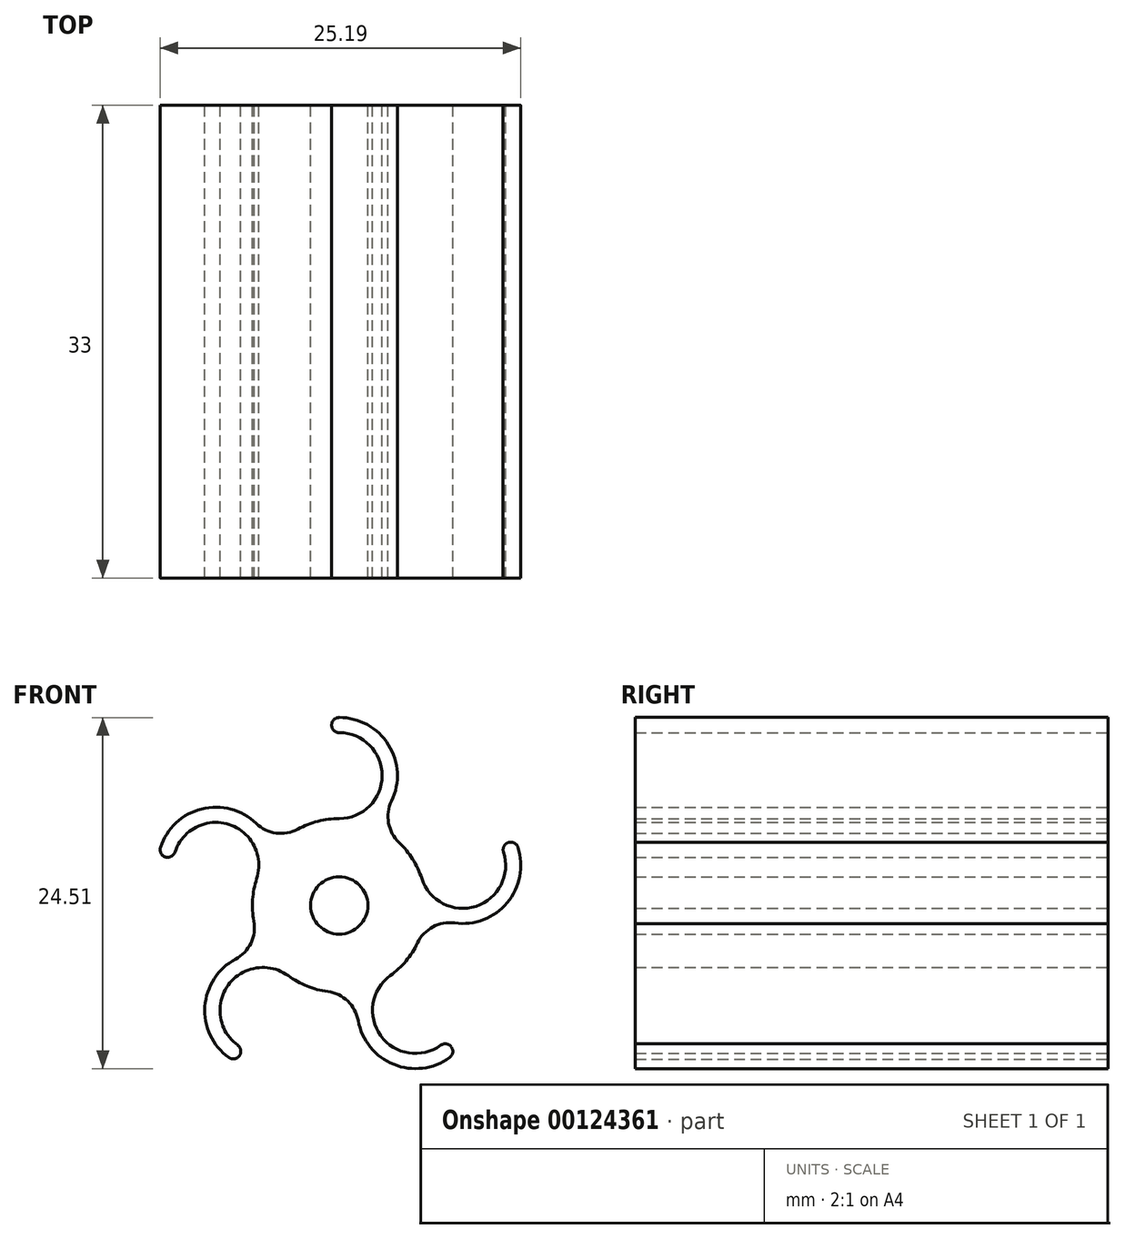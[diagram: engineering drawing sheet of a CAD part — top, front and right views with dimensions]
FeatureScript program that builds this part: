
annotation { "Feature Type Name" : "Feature", "Feature Type Description" : "" }
export const myFeature = defineFeature(function(context is Context, id is Id, definition is map)
    precondition{}
    {
        {
            var Q0;
            Q0=qCreatedBy(makeId("Front.planeOp"),FACE);
            var sketch = newSketch(context, id + "F0", { "sketchPlane" : qUnion([Q0])});
            skArc(sketch, "E0", {"start": v(0, 6.06) * mm, "mid": v(3, 9.06) * mm, "end": v(0, 12.06) * mm});
            skCircle(sketch, "E1", {"center": v(0, 0) * mm, "radius": 2 * mm});
            skArc(sketch, "E2", {"start": v(0, 6.06) * mm, "mid": v(-1.49, 5.88) * mm, "end": v(-2.88, 5.33) * mm});
            skArc(sketch, "E3", {"start": v(0, 13.13) * mm, "mid": v(-0.53, 12.6) * mm, "end": v(0, 12.06) * mm});
            skArc(sketch, "E4.trimOffspring", {"start": v(3.66, 7.3) * mm, "mid": v(3.44, 11.22) * mm, "end": v(0, 13.12) * mm});
            skPoint(sketch, "E5.visualSharp", {"position": v(2.2, 5.65) * mm});
            skArc(sketch, "E5.filletArc", {"start": v(3.66, 7.3) * mm, "mid": v(3.45, 5.75) * mm, "end": v(4.18, 4.39) * mm});
            skLineSegment(sketch, "E6.trimOffspring", {"start": v(0, 12.06) * mm, "end": v(0, 5) * mm, "construction": true});
            skArc(sketch, "E7.1.0", {"start": v(-12.48, 4.06) * mm, "mid": v(-12.14, 3.39) * mm, "end": v(-11.47, 3.73) * mm});
            skArc(sketch, "E7.1.1", {"start": v(-5.8, 5.73) * mm, "mid": v(-9.6, 6.74) * mm, "end": v(-12.48, 4.06) * mm});
            skArc(sketch, "E7.1.2", {"start": v(-5.77, 1.87) * mm, "mid": v(-7.7, 5.65) * mm, "end": v(-11.47, 3.73) * mm});
            skArc(sketch, "E7.1.3", {"start": v(-5.8, 5.73) * mm, "mid": v(-4.4, 5.06) * mm, "end": v(-2.88, 5.33) * mm});
            skArc(sketch, "E7.2.0", {"start": v(-7.71, -10.62) * mm, "mid": v(-6.97, -10.5) * mm, "end": v(-7.1, -9.76) * mm});
            skArc(sketch, "E7.2.1", {"start": v(-7.24, -3.75) * mm, "mid": v(-9.38, -7.05) * mm, "end": v(-7.71, -10.62) * mm});
            skArc(sketch, "E7.2.2", {"start": v(-3.56, -4.9) * mm, "mid": v(-7.75, -5.57) * mm, "end": v(-7.1, -9.76) * mm});
            skArc(sketch, "E7.2.3", {"start": v(-7.24, -3.75) * mm, "mid": v(-6.17, -2.63) * mm, "end": v(-5.96, -1.1) * mm});
            skArc(sketch, "E7.3.0", {"start": v(7.71, -10.62) * mm, "mid": v(7.83, -9.88) * mm, "end": v(7.1, -9.76) * mm});
            skArc(sketch, "E7.3.1", {"start": v(1.33, -8.05) * mm, "mid": v(3.8, -11.1) * mm, "end": v(7.71, -10.62) * mm});
            skArc(sketch, "E7.3.2", {"start": v(3.56, -4.9) * mm, "mid": v(2.9, -9.1) * mm, "end": v(7.1, -9.76) * mm});
            skArc(sketch, "E7.3.3", {"start": v(1.33, -8.05) * mm, "mid": v(0.6, -6.68) * mm, "end": v(-0.8, -6) * mm});
            skArc(sketch, "E7.4.0", {"start": v(12.48, 4.06) * mm, "mid": v(11.81, 4.4) * mm, "end": v(11.47, 3.73) * mm});
            skArc(sketch, "E7.4.1", {"start": v(8.06, -1.22) * mm, "mid": v(11.73, 0.2) * mm, "end": v(12.48, 4.06) * mm});
            skArc(sketch, "E7.4.2", {"start": v(5.77, 1.87) * mm, "mid": v(9.55, -0.05) * mm, "end": v(11.47, 3.73) * mm});
            skArc(sketch, "E7.4.3", {"start": v(8.06, -1.22) * mm, "mid": v(6.54, -1.5) * mm, "end": v(5.47, -2.62) * mm});
            skArc(sketch, "E8.trimOffspring", {"start": v(-5.77, 1.87) * mm, "mid": v(-6.05, 0.4) * mm, "end": v(-5.96, -1.1) * mm});
            skArc(sketch, "E9.trimOffspring", {"start": v(5.77, 1.87) * mm, "mid": v(5.13, 3.23) * mm, "end": v(4.18, 4.39) * mm});
            skArc(sketch, "E10.trimOffspring", {"start": v(3.56, -4.9) * mm, "mid": v(4.66, -3.88) * mm, "end": v(5.47, -2.62) * mm});
            skArc(sketch, "E11.trimOffspring", {"start": v(-3.56, -4.9) * mm, "mid": v(-2.25, -5.63) * mm, "end": v(-0.8, -6) * mm});
            skCircle(sketch, "E12", {"center": v(0, 0) * mm, "radius": 13.13 * mm, "construction": true});
            skSolve(sketch);
        }
        {
            var Q0;
            Q0=makeQuery(id+"F0.imprint","IMPRINT",FACE,{"disambiguationData":[TD([[makeQuery(id+"F0.imprint","IMPRINT",EDGE,{"derivedFrom":sQuery(id+"F0.wireOp",EDGE,"E0")}),-1.0]])]});
            extrude(context, id + "F1", {"entities" : qUnion([Q0]), "depth" : 33 * mm});
        }
    });
